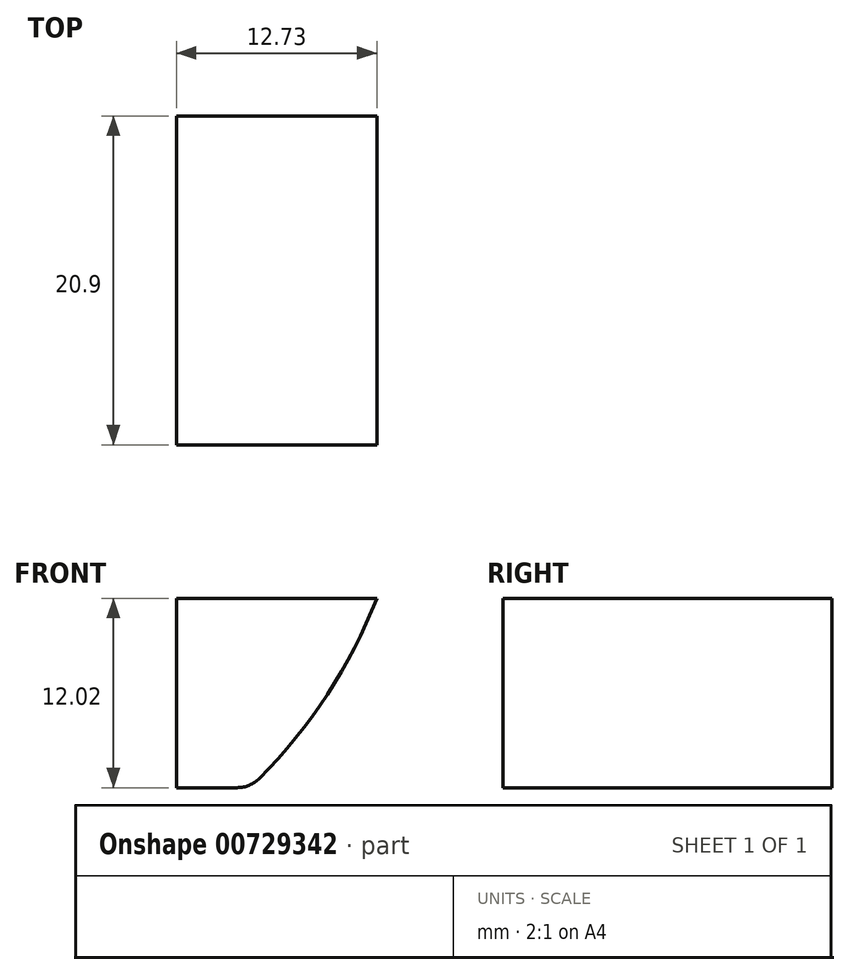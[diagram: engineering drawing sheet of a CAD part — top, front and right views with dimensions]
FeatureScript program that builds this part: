
annotation { "Feature Type Name" : "Feature", "Feature Type Description" : "" }
export const myFeature = defineFeature(function(context is Context, id is Id, definition is map)
    precondition{}
    {
        {
            var Q0;
            Q0=qCreatedBy(makeId("Front.planeOp"),FACE);
            var sketch = newSketch(context, id + "F0", { "sketchPlane" : qUnion([Q0])});
            skLineSegment(sketch, "E0", {"start": v(0, 0) * mm, "end": v(0, 12.02) * mm});
            skLineSegment(sketch, "E1", {"start": v(0, 12.02) * mm, "end": v(12.73, 12.02) * mm});
            skLineSegment(sketch, "E2", {"start": v(0, 0) * mm, "end": v(4.68, 0) * mm});
            skArc(sketch, "E3", {"start": v(4.68, 0) * mm, "mid": v(9.36, 5.57) * mm, "end": v(12.73, 12.02) * mm});
            skSolve(sketch);
        }
        {
            var Q0;
            Q0=makeQuery(id+"F0.imprint","IMPRINT",FACE,{"disambiguationData":[TD([[makeQuery(id+"F0.imprint","IMPRINT",EDGE,{"derivedFrom":sQuery(id+"F0.wireOp",EDGE,"E0")}),-1.0]])]});
            extrude(context, id + "F1", {"entities" : qUnion([Q0]), "depth" : 20.9 * mm, "offsetDistance" : 25 * mm});
        }
        {
            var Q0;
            Q0=makeQuery(id+"F1.opExtrude","SWEPT_EDGE",EDGE,{"disambiguationData":[OSD([sQuery(id+"F0.wireOp",EDGE,"E2"),sQuery(id+"F0.wireOp",EDGE,"E3")])]});
            fillet(context, id + "F2", {"entities" : qUnion([Q0]), "radius" : 2 * mm, "tangentPropagation" : true, "allowEdgeOverflow" : false});
        }
    });
